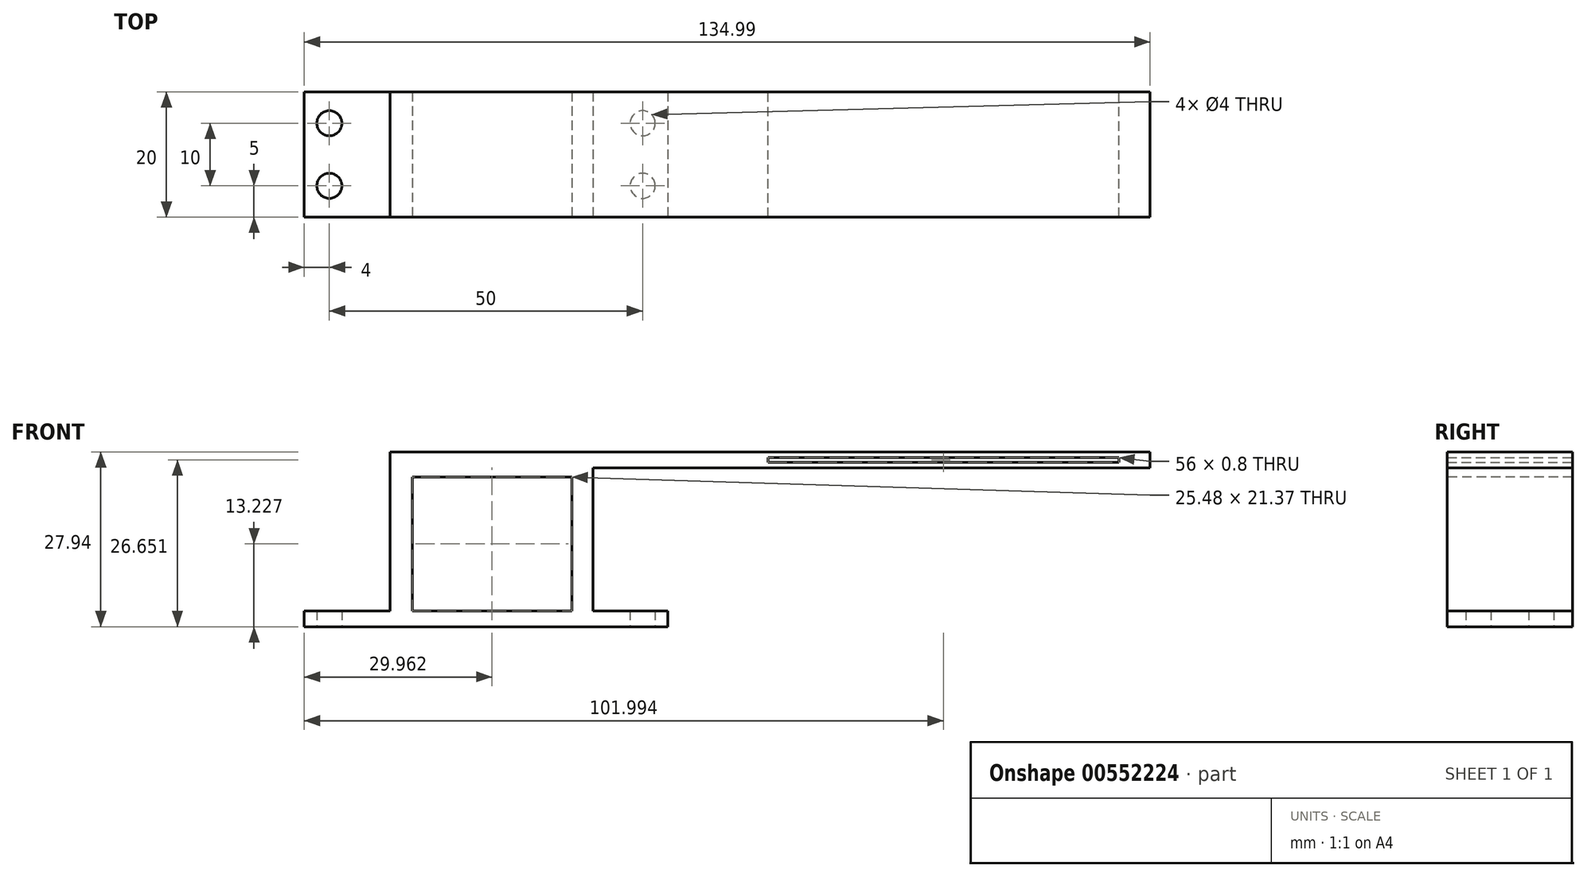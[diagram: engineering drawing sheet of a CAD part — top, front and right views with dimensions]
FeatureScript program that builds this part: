
annotation { "Feature Type Name" : "Feature", "Feature Type Description" : "" }
export const myFeature = defineFeature(function(context is Context, id is Id, definition is map)
    precondition{}
    {
        {
            var Q0;
            Q0=qCreatedBy(makeId("Top.planeOp"),FACE);
            var sketch = newSketch(context, id + "F0", { "sketchPlane" : qUnion([Q0])});
            skLineSegment(sketch, "E0.bottom", {"start": v(-29, 10) * mm, "end": v(29, 10) * mm});
            skLineSegment(sketch, "E0.top", {"start": v(-29, -10) * mm, "end": v(29, -10) * mm});
            skLineSegment(sketch, "E0.left", {"start": v(-29, 10) * mm, "end": v(-29, -10) * mm});
            skLineSegment(sketch, "E0.right", {"start": v(29, 10) * mm, "end": v(29, -10) * mm});
            skCircle(sketch, "E1", {"center": v(-25, 5) * mm, "radius": 2 * mm});
            skCircle(sketch, "E2", {"center": v(-25, -5) * mm, "radius": 2 * mm});
            skCircle(sketch, "E3", {"center": v(25, 5) * mm, "radius": 2 * mm});
            skCircle(sketch, "E4", {"center": v(25, -5) * mm, "radius": 2 * mm});
            skSolve(sketch);
        }
        {
            var Q0;
            Q0 = qSketchRegion(id + "F0", true);
            extrude(context, id + "F1", {"entities" : qUnion([Q0]), "depth" : 2.54 * mm, "offsetDistance" : 25.4 * mm});
        }
        {
            var Q0;
            Q0=makeQuery(id+"F1.opExtrude","CAP_FACE",FACE,{"disambiguationData":[OSD([sQuery(id+"F0.wireOp",EDGE,"747ac24a-afe5-4b64-999f-19a3d27787b8"),sQuery(id+"F0.wireOp",EDGE,"5c8f7829-6496-412c-866f-dbe53b567064"),sQuery(id+"F0.wireOp",EDGE,"ef2c8e1f-5198-447a-a13a-cbf40e058c80"),sQuery(id+"F0.wireOp",EDGE,"5ca80856-a312-4663-bb65-8766e3786a1f"),sQuery(id+"F0.wireOp",EDGE,"E0.bottom"),sQuery(id+"F0.wireOp",EDGE,"E0.top"),sQuery(id+"F0.wireOp",EDGE,"E0.left"),sQuery(id+"F0.wireOp",EDGE,"E0.right")])],"isStart":false});
            var sketch = newSketch(context, id + "F2", { "sketchPlane" : qUnion([Q0])});
            skLineSegment(sketch, "E5.bottom", {"start": v(-15.3, 10) * mm, "end": v(17.1, 10) * mm});
            skLineSegment(sketch, "E5.top", {"start": v(-15.3, -10) * mm, "end": v(17.1, -10) * mm});
            skLineSegment(sketch, "E5.left", {"start": v(-15.3, 10) * mm, "end": v(-15.3, -10) * mm});
            skLineSegment(sketch, "E5.right", {"start": v(17.1, 10) * mm, "end": v(17.1, -10) * mm});
            skSolve(sketch);
        }
        {
            var Q0;
            Q0=makeQuery(id+"F2.imprint","IMPRINT",FACE,{"disambiguationData":[TD([[makeQuery(id+"F2.imprint","IMPRINT",EDGE,{"derivedFrom":sQuery(id+"F2.wireOp",EDGE,"E5.bottom")}),-1.0]])]});
            extrude(context, id + "F3", {"entities" : qUnion([Q0]), "operationType" : NewBodyOperationType.ADD, "depth" : 25.4 * mm, "offsetDistance" : 25.4 * mm});
        }
        {
            var Q0;
            Q0=makeQuery(id+"F3.opExtrude","SWEPT_FACE",FACE,{"disambiguationData":[OSD([sQuery(id+"F2.wireOp",EDGE,"E5.right")])]});
            var sketch = newSketch(context, id + "F4", { "sketchPlane" : qUnion([Q0])});
            skLineSegment(sketch, "E6.bottom", {"start": v(10, 27.94) * mm, "end": v(-10, 27.94) * mm});
            skLineSegment(sketch, "E6.top", {"start": v(10, 25.4) * mm, "end": v(-10, 25.4) * mm});
            skLineSegment(sketch, "E6.left", {"start": v(10, 27.94) * mm, "end": v(10, 25.4) * mm});
            skLineSegment(sketch, "E6.right", {"start": v(-10, 27.94) * mm, "end": v(-10, 25.4) * mm});
            skSolve(sketch);
        }
        {
            var Q0;
            Q0=makeQuery(id+"F4.imprint","IMPRINT",FACE,{"disambiguationData":[TD([[makeQuery(id+"F4.imprint","IMPRINT",EDGE,{"derivedFrom":sQuery(id+"F4.wireOp",EDGE,"E6.bottom")}),1.0]])]});
            extrude(context, id + "F5", {"entities" : qUnion([Q0]), "operationType" : NewBodyOperationType.ADD, "depth" : 88.9 * mm, "offsetDistance" : 25.4 * mm});
        }
        {
            var Q0;
            Q0=makeQuery(id+"F5.boolean.opBoolean","MERGE",FACE,{"derivedFrom":[makeQuery(id+"F3.boolean.opBoolean","MERGE",FACE,{"derivedFrom":[makeQuery(id+"F1.opExtrude","SWEPT_FACE",FACE,{"disambiguationData":[OSD([sQuery(id+"F0.wireOp",EDGE,"E0.bottom")])]}),makeQuery(id+"F3.opExtrude","SWEPT_FACE",FACE,{"disambiguationData":[OSD([sQuery(id+"F2.wireOp",EDGE,"E5.bottom")])]})]}),makeQuery(id+"F5.opExtrude","SWEPT_FACE",FACE,{"disambiguationData":[OSD([sQuery(id+"F4.wireOp",EDGE,"E6.left")])]})]});
            var sketch = newSketch(context, id + "F6", { "sketchPlane" : qUnion([Q0])});
            skLineSegment(sketch, "E7.bottom", {"start": v(-101, 27.05) * mm, "end": v(-45, 27.05) * mm});
            skLineSegment(sketch, "E7.top", {"start": v(-101, 26.25) * mm, "end": v(-45, 26.25) * mm});
            skLineSegment(sketch, "E7.left", {"start": v(-101, 27.05) * mm, "end": v(-101, 26.25) * mm});
            skLineSegment(sketch, "E7.right", {"start": v(-45, 27.05) * mm, "end": v(-45, 26.25) * mm});
            skSolve(sketch);
        }
        {
            var Q0;
            Q0=makeQuery(id+"F6.imprint","IMPRINT",FACE,{"disambiguationData":[TD([[makeQuery(id+"F6.imprint","IMPRINT",EDGE,{"derivedFrom":sQuery(id+"F6.wireOp",EDGE,"E7.bottom")}),-1.0]])]});
            extrude(context, id + "F7", {"entities" : qUnion([Q0]), "operationType" : NewBodyOperationType.REMOVE, "endBound" : BoundingType.THROUGH_ALL, "oppositeDirection" : true, "depth" : 25.4 * mm, "offsetDistance" : 25.4 * mm});
        }
        {
            var Q0;
            Q0=makeQuery(id+"F5.boolean.opBoolean","MERGE",FACE,{"derivedFrom":[makeQuery(id+"F3.boolean.opBoolean","MERGE",FACE,{"derivedFrom":[makeQuery(id+"F1.opExtrude","SWEPT_FACE",FACE,{"disambiguationData":[OSD([sQuery(id+"F0.wireOp",EDGE,"E0.top")])]}),makeQuery(id+"F3.opExtrude","SWEPT_FACE",FACE,{"disambiguationData":[OSD([sQuery(id+"F2.wireOp",EDGE,"E5.top")])]})]}),makeQuery(id+"F5.opExtrude","SWEPT_FACE",FACE,{"disambiguationData":[OSD([sQuery(id+"F4.wireOp",EDGE,"E6.right")])]})]});
            var sketch = newSketch(context, id + "F8", { "sketchPlane" : qUnion([Q0])});
            skLineSegment(sketch, "E8.bottom", {"start": v(-11.78, 2.54) * mm, "end": v(13.7, 2.54) * mm});
            skLineSegment(sketch, "E8.top", {"start": v(-11.78, 23.91) * mm, "end": v(13.7, 23.91) * mm});
            skLineSegment(sketch, "E8.left", {"start": v(-11.78, 2.54) * mm, "end": v(-11.78, 23.91) * mm});
            skLineSegment(sketch, "E8.right", {"start": v(13.7, 2.54) * mm, "end": v(13.7, 23.91) * mm});
            skSolve(sketch);
        }
        {
            var Q0;
            Q0 = qSketchRegion(id + "F8", true);
            extrude(context, id + "F9", {"entities" : qUnion([Q0]), "operationType" : NewBodyOperationType.REMOVE, "endBound" : BoundingType.THROUGH_ALL, "oppositeDirection" : true, "depth" : 25 * mm, "offsetDistance" : 25 * mm});
        }
    });
